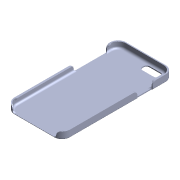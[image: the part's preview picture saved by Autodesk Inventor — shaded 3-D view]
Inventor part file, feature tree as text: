
AUTODESK INVENTOR PART (.ipt)
format: ipt  version: 2015 (Build 190159000, 159)  size: 215,552 bytes
history: native  units: mm (DEFAULTED — no unit token found)
features: fillet x1, other x1, imported_body x1
ambient origin geometry x8: Origin, YZ Plane, XZ Plane, XY Plane, X Axis, Y Axis, Z Axis, Center Point
bodies: Body1 (feature_tree)
feature tree (3):
  fillet  "Fillet30"  [1 undecoded]
  other  "iphone_6_case_v31"
  imported_body  "Base1"
note: 1 required parameter value undecoded (feature->parameter linkage not recoverable at this tier; creation-order binding heuristic only, values carry confidence <= 0.55)
